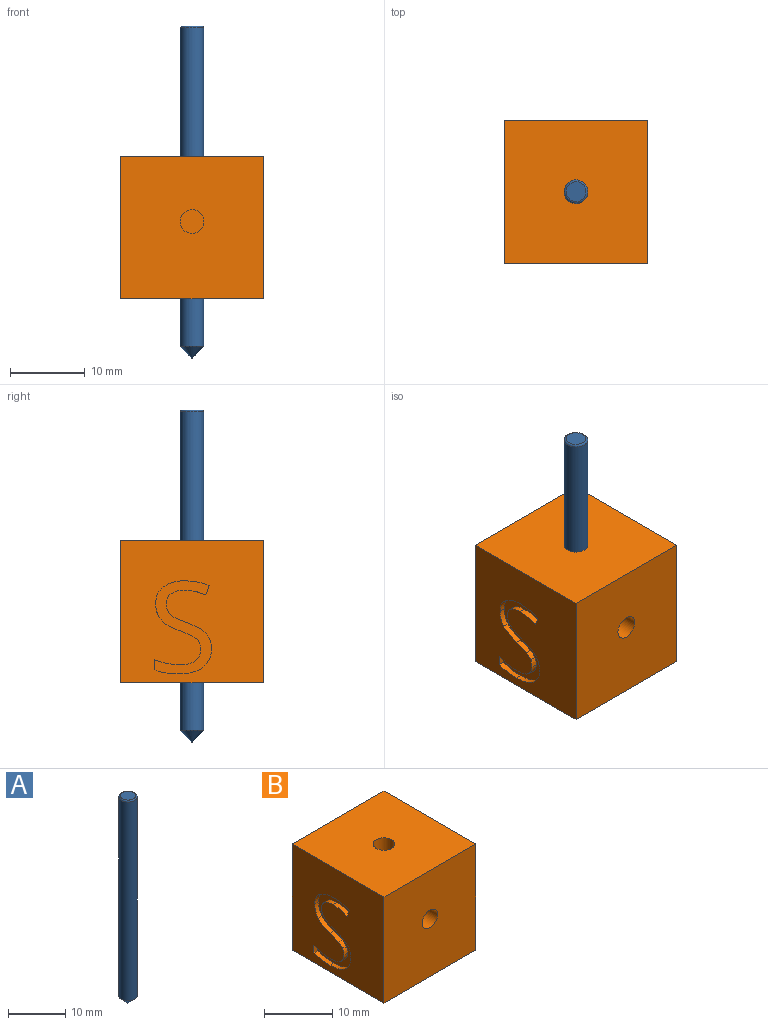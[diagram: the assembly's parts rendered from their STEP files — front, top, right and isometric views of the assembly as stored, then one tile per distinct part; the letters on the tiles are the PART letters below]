
ASSEMBLY  parts=2 mates=1
PART A: 5 faces, bbox 3.4x3.4x44.5 mm
  f0: cylinder r=1.59mm len=42.62mm, axis (0,0,-1), area 425.1mm2, adj f3,f4
  f1: plane 2.67x2.67mm, normal (0,0,1), area 5.6mm2, adj f4
  f2: plane 0.03x0.03mm, normal (0,0,-1), area 0mm2, adj f3
  f3: cone r=1.59mm half-angle=45deg, axis (0,0,1), area 11.2mm2, adj f0,f2
  f4: torus R=1.33mm, axis (0,0,1), area 3.7mm2, adj f0,f1
PART B: 70 faces, bbox 19.1x19.1x19.1 mm
  f0: plane 19.05x19.05mm, normal (-1,0,0), area 328.8mm2, adj f1,f3,f4,f5,f44,f45,f46,f47
  f1: plane 19.05x19.05mm, normal (0,1,0), area 300.4mm2, adj f0,f2,f4,f5,f24,f25,f26,f27
  f2: plane 19.05x19.05mm, normal (1,0,0), area 333.2mm2, adj f1,f3,f4,f5,f9,f10,f11,f12
  f3: plane 19.05x19.05mm, normal (0,-1,0), area 355mm2, adj f0,f2,f4,f5,f7
  f4: plane 19.05x19.05mm, normal (0,0,1), area 355mm2, adj f0,f1,f2,f3,f6
  f5: plane 19.05x19.05mm, normal (0,0,-1), area 355mm2, adj f0,f1,f2,f3,f6
  f6: cylinder r=1.59mm len=19.05mm, axis (0,0,-1), area 190mm2, adj f4,f5
  f7: cylinder r=1.59mm len=6.35mm, axis (0,-1,0), area 63.3mm2, adj f3,f8
  f8: plane 3.18x3.18mm, normal (0,-1,0), area 7.9mm2, adj f7
  f9: plane 1.15x0.79mm, normal (0,0,1), area 0.9mm2, adj f2,f10,f21,f22
  f10: plane 9.57x3.75mm, normal (0,-0.93,-0.36), area 8.2mm2, adj f2,f9,f11,f22
  f11: plane 0.93x0.79mm, normal (0,0,-1), area 0.7mm2, adj f2,f10,f12,f22
  f12: plane 9.57x3.77mm, normal (0,0.93,-0.37), area 8.2mm2, adj f2,f11,f13,f22
  f13: plane 1.12x0.79mm, normal (0,0,1), area 0.9mm2, adj f2,f12,f14,f22
  f14: plane 3.03x1.17mm, normal (0,-0.93,0.36), area 2.6mm2, adj f2,f13,f15,f22
  f15: plane 3.82x0.79mm, normal (0,0,1), area 3mm2, adj f2,f14,f21,f22
  f16: plane 3.08x0.79mm, normal (0,0,-1), area 2.4mm2, adj f17,f20,f22,f23
  f17: plane 2.95x1.12mm, normal (0,-0.94,0.35), area 2.5mm2, adj f16,f18,f22,f23
  f18: extruded ~1.38x0.79mm, area 1.1mm2, adj f17,f19,f22,f23
  f19: extruded ~1.38x0.79mm, area 1.1mm2, adj f18,f20,f22,f23
  f20: plane 2.95x1.11mm, normal (0,0.94,0.35), area 2.5mm2, adj f16,f19,f22,f23
  f21: plane 3.03x1.19mm, normal (0,0.93,0.36), area 2.6mm2, adj f2,f9,f15,f22
  f22: plane 9.57x8.45mm, normal (1,0,0), area 23.4mm2, adj f9,f10,f11,f12,f13,f14,f15,f16
  f23: plane 4.33x3.08mm, normal (1,0,0), area 6.4mm2, adj f16,f17,f18,f19,f20
  f24: plane 2.5x0.79mm, normal (0,0,1), area 2mm2, adj f1,f25,f41,f42
  f25: plane 4.97x2.89mm, normal (-0.86,0,0.5), area 4.6mm2, adj f1,f24,f26,f42
  f26: plane 1.64x0.79mm, normal (0,0,1), area 1.3mm2, adj f1,f25,f27,f42
  f27: plane 5.37x3.25mm, normal (0.86,0,-0.52), area 5mm2, adj f1,f26,f28,f42
  f28: extruded ~3.2x2.4mm, area 3.4mm2, adj f1,f27,f29,f42
  f29: extruded ~2.53x1.05mm, area 2.3mm2, adj f1,f28,f30,f42
  f30: extruded ~3.25x0.84mm, area 2.7mm2, adj f1,f29,f31,f42
  f31: plane 3.28x0.79mm, normal (0,0,-1), area 2.6mm2, adj f1,f30,f32,f42
  f32: plane 11.95x0.79mm, normal (-1,0,0), area 9.5mm2, adj f1,f31,f33,f42
  f33: plane 1.39x0.79mm, normal (0,0,1), area 1.1mm2, adj f1,f32,f41,f42
  f34: plane 4.57x0.79mm, normal (1,0,0), area 3.6mm2, adj f35,f40,f42,f43
  f35: plane 1.81x0.79mm, normal (0,0,1), area 1.4mm2, adj f34,f36,f42,f43
  f36: extruded ~2.24x0.79mm, area 1.9mm2, adj f35,f37,f42,f43
  f37: extruded ~1.71x0.79mm, area 1.5mm2, adj f36,f38,f42,f43
  f38: extruded ~1.75x0.79mm, area 1.5mm2, adj f37,f39,f42,f43
  f39: extruded ~2.16x0.79mm, area 1.8mm2, adj f38,f40,f42,f43
  f40: plane 1.91x0.79mm, normal (0,0,-1), area 1.5mm2, adj f34,f39,f42,f43
  f41: plane 4.97x0.79mm, normal (1,0,0), area 3.9mm2, adj f1,f24,f33,f42
  f42: plane 11.95x8.42mm, normal (0,1,0), area 42.8mm2, adj f24,f25,f26,f27,f28,f29,f30,f31
  f43: plane 4.75x4.57mm, normal (0,1,0), area 19.6mm2, adj f34,f35,f36,f37,f38,f39,f40
  f44: extruded ~2.02x0.79mm, area 1.7mm2, adj f0,f45,f68,f69
  f45: extruded ~2.63x1.46mm, area 2.4mm2, adj f0,f44,f46,f69
  f46: extruded ~1.69x0.79mm, area 1.5mm2, adj f0,f45,f47,f69
  f47: extruded ~0.79x0.79mm, area 0.9mm2, adj f0,f46,f48,f69
  f48: extruded ~1.03x0.79mm, area 0.9mm2, adj f0,f47,f49,f69
  f49: extruded ~1.34x0.79mm, area 1.2mm2, adj f0,f48,f50,f69
  f50: extruded ~1.75x0.79mm, area 1.5mm2, adj f0,f49,f51,f69
  f51: extruded ~2.92x0.79mm, area 2.4mm2, adj f0,f50,f52,f69
  f52: plane 1.23x0.79mm, normal (0,0.94,0.34), area 1mm2, adj f0,f51,f53,f69
  f53: extruded ~3.33x0.79mm, area 2.7mm2, adj f0,f52,f54,f69
  f54: extruded ~2.79x0.83mm, area 2.4mm2, adj f0,f53,f55,f69
  f55: extruded ~2.23x1.05mm, area 2mm2, adj f0,f54,f56,f69
  f56: extruded ~2.17x0.79mm, area 1.9mm2, adj f0,f55,f57,f69
  f57: extruded ~2.42x1.44mm, area 2.3mm2, adj f0,f56,f58,f69
  f58: extruded ~1.81x0.79mm, area 1.6mm2, adj f0,f57,f59,f69
  f59: extruded ~0.85x0.79mm, area 0.9mm2, adj f0,f58,f60,f69
  f60: extruded ~1.03x0.79mm, area 0.9mm2, adj f0,f59,f61,f69
  f61: extruded ~1.49x0.79mm, area 1.4mm2, adj f0,f60,f62,f69
  f62: extruded ~2.13x0.79mm, area 1.8mm2, adj f0,f61,f63,f69
  f63: extruded ~1.74x0.79mm, area 1.4mm2, adj f0,f62,f64,f69
  f64: extruded ~1.63x0.79mm, area 1.4mm2, adj f0,f63,f65,f69
  f65: plane 1.36x0.79mm, normal (0,-1,0), area 1.1mm2, adj f0,f64,f66,f69
  f66: extruded ~3.32x0.79mm, area 2.7mm2, adj f0,f65,f67,f69
  f67: extruded ~3.16x0.9mm, area 2.7mm2, adj f0,f66,f68,f69
  f68: extruded ~2.5x1.16mm, area 2.3mm2, adj f0,f44,f67,f69
  f69: plane 12.48x7.64mm, normal (-1,0,0), area 34.1mm2, adj f44,f45,f46,f47,f48,f49,f50,f51
PLACE A t=(-2.56,5.78,34.7)mm
PLACE B t=(-2.56,5.78,42.62)mm
MATE slider B.f6 <-> A.f0  axis (0,0,-1) through (-2.56,5.78,61.67)mm
